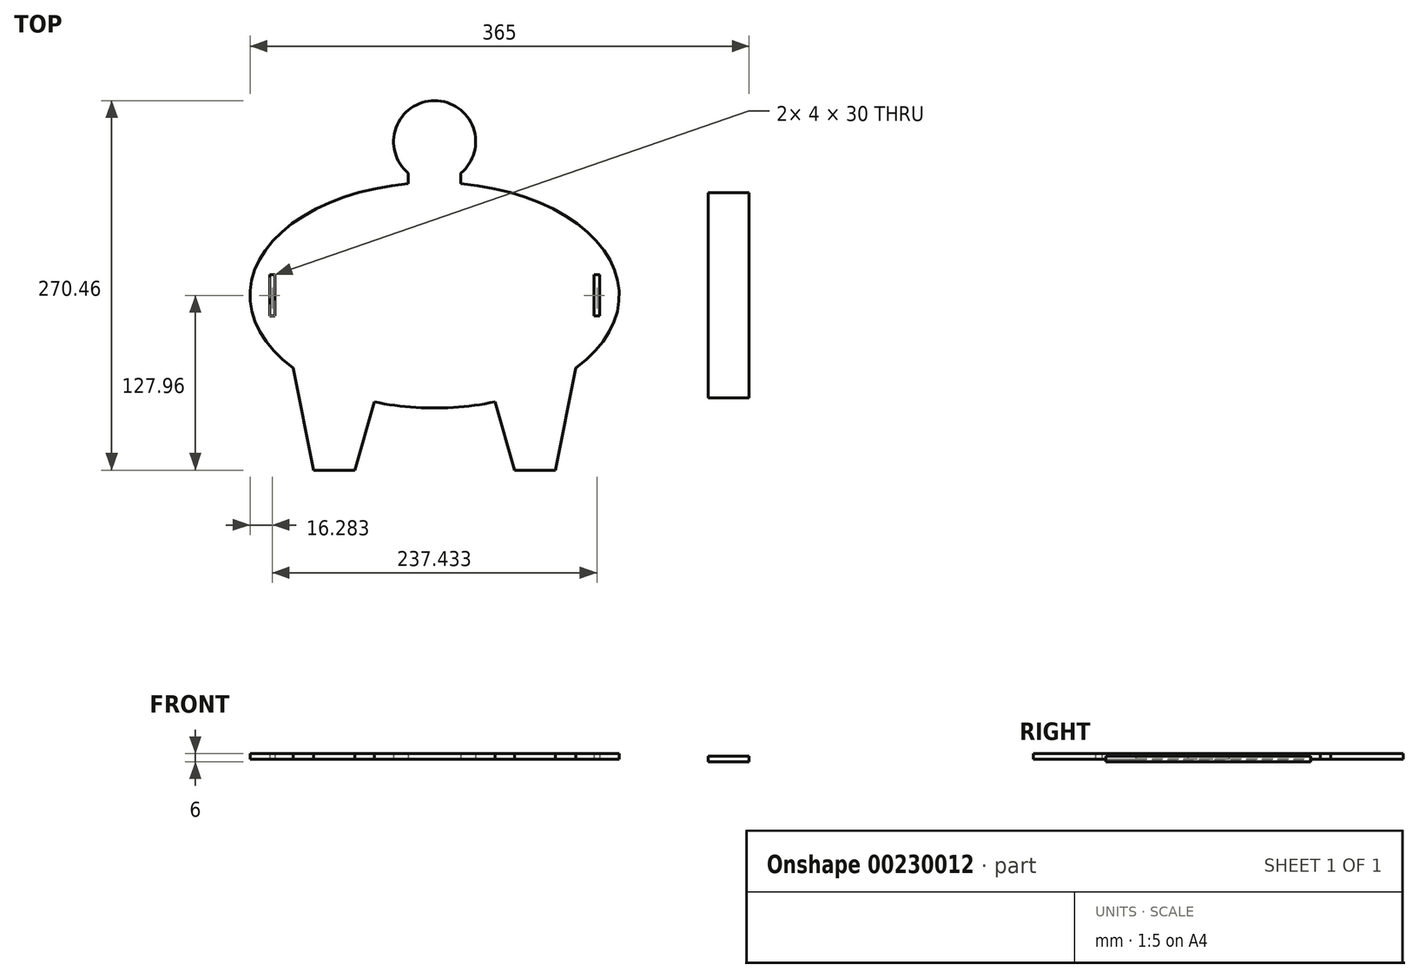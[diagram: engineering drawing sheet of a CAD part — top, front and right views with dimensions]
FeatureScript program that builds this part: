
annotation { "Feature Type Name" : "Feature", "Feature Type Description" : "" }
export const myFeature = defineFeature(function(context is Context, id is Id, definition is map)
    precondition{}
    {
        {
            var Q0;
            Q0=qCreatedBy(makeId("Top.planeOp"),FACE);
            var sketch = newSketch(context, id + "F0", { "sketchPlane" : qUnion([Q0])});
            skEllipse(sketch, "E0", {"center": v(0, 0) * mm, "majorRadius": 135 * mm, "minorRadius": 82.5 * mm, "majorAxis": v(1, 0)});
            skFitSpline(sketch, "E1.0", {"points": [v(104.96, -1.66) * mm, v(105.02, 0) * mm, v(104.96, 1.66) * mm, v(104.68, 3.9) * mm, v(103.99, 6.8) * mm, v(102.45, 10.58) * mm, v(100.05, 14.7) * mm, v(96.68, 19.09) * mm, v(92.97, 22.89) * mm, v(89.46, 25.95) * mm, v(86.54, 28.24) * mm, v(83.87, 30.13) * mm, v(81.6, 31.63) * mm, v(79.83, 32.74) * mm, v(77.99, 33.84) * mm, v(75.46, 35.27) * mm, v(72.16, 37) * mm, v(67.99, 39) * mm, v(62.15, 41.5) * mm, v(54.38, 44.35) * mm, v(44.4, 47.23) * mm, v(33.86, 49.54) * mm, v(24.7, 50.95) * mm, v(17.22, 51.75) * mm, v(11.54, 52.18) * mm, v(6.75, 52.4) * mm, v(2.9, 52.49) * mm, v(0, 52.5) * mm, v(-2.9, 52.49) * mm, v(-6.75, 52.4) * mm, v(-11.54, 52.18) * mm, v(-17.22, 51.75) * mm, v(-24.7, 50.95) * mm, v(-33.86, 49.54) * mm, v(-44.4, 47.23) * mm, v(-54.38, 44.35) * mm, v(-62.15, 41.5) * mm, v(-67.99, 39) * mm, v(-72.16, 37) * mm, v(-75.46, 35.27) * mm, v(-77.99, 33.84) * mm, v(-79.83, 32.74) * mm, v(-81.6, 31.63) * mm, v(-83.87, 30.13) * mm, v(-86.54, 28.24) * mm, v(-89.46, 25.95) * mm, v(-92.97, 22.89) * mm, v(-96.68, 19.09) * mm, v(-100.05, 14.7) * mm, v(-102.45, 10.58) * mm, v(-103.99, 6.8) * mm, v(-104.68, 3.9) * mm, v(-104.96, 1.66) * mm, v(-105.02, 0) * mm, v(-104.96, -1.66) * mm, v(-104.68, -3.9) * mm, v(-103.99, -6.8) * mm, v(-102.45, -10.58) * mm, v(-100.05, -14.7) * mm, v(-96.68, -19.09) * mm, v(-92.97, -22.89) * mm, v(-89.46, -25.95) * mm, v(-86.54, -28.24) * mm, v(-83.87, -30.13) * mm, v(-81.6, -31.63) * mm, v(-79.83, -32.74) * mm, v(-77.99, -33.84) * mm, v(-75.46, -35.27) * mm, v(-72.16, -37) * mm, v(-67.99, -39) * mm, v(-62.15, -41.5) * mm, v(-54.38, -44.35) * mm, v(-44.4, -47.23) * mm, v(-33.86, -49.54) * mm, v(-24.7, -50.95) * mm, v(-17.22, -51.75) * mm, v(-11.54, -52.18) * mm, v(-6.75, -52.4) * mm, v(-2.9, -52.49) * mm, v(0, -52.5) * mm, v(2.9, -52.49) * mm, v(6.75, -52.4) * mm, v(11.54, -52.18) * mm, v(17.22, -51.75) * mm, v(24.7, -50.95) * mm, v(33.86, -49.54) * mm, v(44.4, -47.23) * mm, v(54.38, -44.35) * mm, v(62.15, -41.5) * mm, v(67.99, -39) * mm, v(72.16, -37) * mm, v(75.46, -35.27) * mm, v(77.99, -33.84) * mm, v(79.83, -32.74) * mm, v(81.6, -31.63) * mm, v(83.87, -30.13) * mm, v(86.54, -28.24) * mm, v(89.46, -25.95) * mm, v(92.97, -22.89) * mm, v(96.68, -19.09) * mm, v(100.05, -14.7) * mm, v(102.45, -10.58) * mm, v(103.99, -6.8) * mm, v(104.68, -3.9) * mm, v(104.96, -1.66) * mm, v(105.02, 0) * mm, v(104.96, 1.66) * mm, v(104.96, -1.66) * mm]});
            skLineSegment(sketch, "E2.bottom", {"start": v(150, 150) * mm, "end": v(-150, 150) * mm});
            skLineSegment(sketch, "E2.top", {"start": v(150, -150) * mm, "end": v(-150, -150) * mm});
            skLineSegment(sketch, "E2.left", {"start": v(150, 150) * mm, "end": v(150, -150) * mm});
            skLineSegment(sketch, "E2.right", {"start": v(-150, 150) * mm, "end": v(-150, -150) * mm});
            skLineSegment(sketch, "E3", {"start": v(0, 0) * mm, "end": v(0, 150) * mm, "construction": true});
            skLineSegment(sketch, "E4.1.0", {"start": v(0, 0) * mm, "end": v(-129.9, -75) * mm, "construction": true});
            skLineSegment(sketch, "E4.2.0", {"start": v(0, 0) * mm, "end": v(129.9, -75) * mm, "construction": true});
            skCircle(sketch, "E5", {"center": v(0, 112.5) * mm, "radius": 30 * mm});
            skCircle(sketch, "E6", {"center": v(70.15, -40.5) * mm, "radius": 30 * mm});
            skLineSegment(sketch, "E7", {"start": v(0, 150) * mm, "end": v(0, -150) * mm, "construction": true});
            skCircle(sketch, "E8.MirrorC", {"center": v(-70.15, -40.5) * mm, "radius": 30 * mm});
            skLineSegment(sketch, "E9.bottom", {"start": v(-30, 50.1) * mm, "end": v(30, 50.1) * mm});
            skLineSegment(sketch, "E9.top", {"start": v(-30, -24.9) * mm, "end": v(30, -24.9) * mm});
            skLineSegment(sketch, "E9.left", {"start": v(-30, 50.1) * mm, "end": v(-30, -24.9) * mm});
            skLineSegment(sketch, "E9.right", {"start": v(30, 50.1) * mm, "end": v(30, -24.9) * mm});
            skLineSegment(sketch, "E10.top", {"start": v(103.41, -127.96) * mm, "end": v(43.41, -127.96) * mm, "construction": true});
            skLineSegment(sketch, "E10.left", {"start": v(103.41, -53.03) * mm, "end": v(103.41, -127.96) * mm, "construction": true});
            skLineSegment(sketch, "E11.trimOffspring", {"start": v(44.17, -77.96) * mm, "end": v(43.41, -127.96) * mm, "construction": true});
            skLineSegment(sketch, "E12", {"start": v(73.41, -127.96) * mm, "end": v(73.41, -69.24) * mm, "construction": true});
            skPoint(sketch, "E13", {"position": v(58.41, -127.96) * mm});
            skPoint(sketch, "E14", {"position": v(88.41, -127.96) * mm});
            skLineSegment(sketch, "E15", {"start": v(44.17, -77.96) * mm, "end": v(58.41, -127.96) * mm});
            skLineSegment(sketch, "E16", {"start": v(88.41, -127.96) * mm, "end": v(103.41, -53.03) * mm});
            skLineSegment(sketch, "E17", {"start": v(58.41, -127.96) * mm, "end": v(88.41, -127.96) * mm});
            skLineSegment(sketch, "E18.MirrorCS", {"start": v(-58.41, -127.96) * mm, "end": v(-88.41, -127.96) * mm});
            skLineSegment(sketch, "E19.MirrorCS", {"start": v(-103.41, -127.96) * mm, "end": v(-43.41, -127.96) * mm, "construction": true});
            skLineSegment(sketch, "E20.MirrorCS", {"start": v(-73.41, -127.96) * mm, "end": v(-73.41, -69.24) * mm, "construction": true});
            skLineSegment(sketch, "E21.MirrorCS", {"start": v(-44.17, -77.96) * mm, "end": v(-58.41, -127.96) * mm});
            skPoint(sketch, "E22.MirrorP", {"position": v(-58.41, -127.96) * mm});
            skLineSegment(sketch, "E23.MirrorCS", {"start": v(-44.17, -77.96) * mm, "end": v(-43.41, -127.96) * mm, "construction": true});
            skPoint(sketch, "E24.MirrorP", {"position": v(-88.41, -127.96) * mm});
            skLineSegment(sketch, "E25.MirrorCS", {"start": v(-88.41, -127.96) * mm, "end": v(-103.41, -53.03) * mm});
            skLineSegment(sketch, "E26.MirrorCS", {"start": v(-103.41, -53.03) * mm, "end": v(-103.41, -127.96) * mm, "construction": true});
            skLineSegment(sketch, "E27.bottom", {"start": v(-150, 150) * mm, "end": v(150, 150) * mm});
            skLineSegment(sketch, "E27.top", {"start": v(-150, -150) * mm, "end": v(150, -150) * mm});
            skLineSegment(sketch, "E28", {"start": v(-19.17, 89.43) * mm, "end": v(-19.17, 81.66) * mm});
            skLineSegment(sketch, "E29.MirrorCS", {"start": v(19.17, 89.43) * mm, "end": v(19.17, 81.66) * mm});
            skLineSegment(sketch, "E30.bottom", {"start": v(-116.72, 15) * mm, "end": v(-120.72, 15) * mm});
            skLineSegment(sketch, "E30.top", {"start": v(-116.72, -15) * mm, "end": v(-120.72, -15) * mm});
            skLineSegment(sketch, "E30.left", {"start": v(-116.72, 15) * mm, "end": v(-116.72, -15) * mm});
            skLineSegment(sketch, "E30.right", {"start": v(-120.72, 15) * mm, "end": v(-120.72, -15) * mm});
            skPoint(sketch, "E30.middle", {"position": v(-118.72, 0) * mm});
            skLineSegment(sketch, "E31.MirrorCS", {"start": v(116.72, -15) * mm, "end": v(120.72, -15) * mm});
            skLineSegment(sketch, "E32.MirrorCS", {"start": v(116.72, 15) * mm, "end": v(120.72, 15) * mm});
            skPoint(sketch, "E33.MirrorP", {"position": v(118.72, 0) * mm});
            skLineSegment(sketch, "E34.MirrorCS", {"start": v(120.72, 15) * mm, "end": v(120.72, -15) * mm});
            skLineSegment(sketch, "E35.MirrorCS", {"start": v(116.72, 15) * mm, "end": v(116.72, -15) * mm});
            skSolve(sketch);
        }
        {
            var Q0;
            Q0=makeQuery(id+"F0.imprint","IMPRINT",FACE,{"disambiguationData":[TD([[makeQuery(id+"F0.imprint","IMPRINT",EDGE,{"derivedFrom":sQuery(id+"F0.wireOp",EDGE,"E5")}),1.0]])]});
            var Q1;
            {var subQ0=sQuery(id+"F0.wireOp",EDGE,"E0");var subQ5=makeQuery(id+"F0.imprint","INTERSECT",VERTEX,{"derivedFrom":[subQ0,sQuery(id+"F0.wireOp",EDGE,"E25.MirrorCS")]});Q1=makeQuery(id+"F0.imprint","IMPRINT",FACE,{"disambiguationData":[TD([[makeQuery(id+"F0.imprint","IMPRINT",EDGE,{"disambiguationData":[TD([[subQ5,1.0]])],"derivedFrom":subQ0}),1.0]])]});}
            var Q2;
            {var subQ0=sQuery(id+"F0.wireOp",EDGE,"E8.MirrorC");var subQ1=sQuery(id+"F0.wireOp",EDGE,"E0");var subQ2=makeQuery(id+"F0.imprint","INTERSECT",VERTEX,{"disambiguationData":[OD(0.0)],"derivedFrom":[subQ1,subQ0]});Q2=makeQuery(id+"F0.imprint","IMPRINT",FACE,{"disambiguationData":[TD([[makeQuery(id+"F0.imprint","IMPRINT",EDGE,{"disambiguationData":[TD([[subQ2,-1.0]])],"derivedFrom":subQ1}),1.0]])]});}
            var Q3;
            {var subQ0=sQuery(id+"F0.wireOp",EDGE,"E8.MirrorC");var subQ1=sQuery(id+"F0.wireOp",EDGE,"E1.0");var subQ2=makeQuery(id+"F0.imprint","INTERSECT",VERTEX,{"disambiguationData":[OD(0.0)],"derivedFrom":[subQ1,subQ0]});Q3=makeQuery(id+"F0.imprint","IMPRINT",FACE,{"disambiguationData":[TD([[makeQuery(id+"F0.imprint","IMPRINT",EDGE,{"disambiguationData":[TD([[subQ2,-1.0]])],"derivedFrom":subQ1}),1.0]])]});}
            var Q4;
            {var subQ0=sQuery(id+"F0.wireOp",EDGE,"E9.bottom");Q4=makeQuery(id+"F0.imprint","IMPRINT",FACE,{"disambiguationData":[TD([[makeQuery(id+"F0.imprint","IMPRINT",EDGE,{"derivedFrom":subQ0}),1.0]])]});}
            var Q5;
            Q5=makeQuery(id+"F0.imprint","IMPRINT",FACE,{"disambiguationData":[TD([[makeQuery(id+"F0.imprint","IMPRINT",EDGE,{"derivedFrom":sQuery(id+"F0.wireOp",EDGE,"E9.bottom")}),-1.0]])]});
            var Q6;
            {var subQ0=sQuery(id+"F0.wireOp",EDGE,"E6");var subQ1=sQuery(id+"F0.wireOp",EDGE,"E1.0");var subQ2=makeQuery(id+"F0.imprint","INTERSECT",VERTEX,{"disambiguationData":[OD(0.0)],"derivedFrom":[subQ1,subQ0]});Q6=makeQuery(id+"F0.imprint","IMPRINT",FACE,{"disambiguationData":[TD([[makeQuery(id+"F0.imprint","IMPRINT",EDGE,{"disambiguationData":[TD([[subQ2,-1.0]])],"derivedFrom":subQ1}),1.0]])]});}
            var Q7;
            {var subQ0=sQuery(id+"F0.wireOp",EDGE,"E6");var subQ1=sQuery(id+"F0.wireOp",EDGE,"E0");var subQ2=makeQuery(id+"F0.imprint","INTERSECT",VERTEX,{"disambiguationData":[OD(0.0)],"derivedFrom":[subQ1,subQ0]});Q7=makeQuery(id+"F0.imprint","IMPRINT",FACE,{"disambiguationData":[TD([[makeQuery(id+"F0.imprint","IMPRINT",EDGE,{"disambiguationData":[TD([[subQ2,-1.0]])],"derivedFrom":subQ1}),1.0]])]});}
            var Q8;
            {var subQ0=sQuery(id+"F0.wireOp",EDGE,"E6");var subQ1=sQuery(id+"F0.wireOp",EDGE,"E0");var subQ2=makeQuery(id+"F0.imprint","INTERSECT",VERTEX,{"disambiguationData":[OD(0.0)],"derivedFrom":[subQ1,subQ0]});Q8=makeQuery(id+"F0.imprint","IMPRINT",FACE,{"disambiguationData":[TD([[makeQuery(id+"F0.imprint","IMPRINT",EDGE,{"disambiguationData":[TD([[subQ2,-1.0]])],"derivedFrom":subQ1}),-1.0]])]});}
            var Q9;
            {var subQ0=sQuery(id+"F0.wireOp",EDGE,"E8.MirrorC");var subQ1=sQuery(id+"F0.wireOp",EDGE,"E0");var subQ2=makeQuery(id+"F0.imprint","INTERSECT",VERTEX,{"disambiguationData":[OD(0.0)],"derivedFrom":[subQ1,subQ0]});Q9=makeQuery(id+"F0.imprint","IMPRINT",FACE,{"disambiguationData":[TD([[makeQuery(id+"F0.imprint","IMPRINT",EDGE,{"disambiguationData":[TD([[subQ2,-1.0]])],"derivedFrom":subQ1}),-1.0]])]});}
            var Q10;
            Q10=makeQuery(id+"F0.imprint","IMPRINT",FACE,{"disambiguationData":[TD([[makeQuery(id+"F0.imprint","IMPRINT",EDGE,{"derivedFrom":sQuery(id+"F0.wireOp",EDGE,"E18.MirrorCS")}),-1.0]])]});
            var Q11;
            {var subQ0=sQuery(id+"F0.wireOp",EDGE,"E15");Q11=makeQuery(id+"F0.imprint","IMPRINT",FACE,{"disambiguationData":[TD([[makeQuery(id+"F0.imprint","IMPRINT",EDGE,{"derivedFrom":subQ0}),1.0]])]});}
            var Q12;
            {var subQ5=sQuery(id+"F0.wireOp",EDGE,"E0");var subQ8=makeQuery(id+"F0.imprint","INTERSECT",VERTEX,{"derivedFrom":[subQ5,sQuery(id+"F0.wireOp",EDGE,"E21.MirrorCS")]});Q12=makeQuery(id+"F0.imprint","IMPRINT",FACE,{"disambiguationData":[TD([[makeQuery(id+"F0.imprint","IMPRINT",EDGE,{"disambiguationData":[TD([[subQ8,1.0]])],"derivedFrom":subQ5}),1.0]])]});}
            var Q13;
            {var subQ0=sQuery(id+"F0.wireOp",EDGE,"E28");Q13=makeQuery(id+"F0.imprint","IMPRINT",FACE,{"disambiguationData":[TD([[makeQuery(id+"F0.imprint","IMPRINT",EDGE,{"derivedFrom":subQ0}),1.0]])]});}
            var Q14;
            {var subQ0=sQuery(id+"F0.wireOp",EDGE,"E29.MirrorCS");Q14=makeQuery(id+"F0.imprint","IMPRINT",FACE,{"disambiguationData":[TD([[makeQuery(id+"F0.imprint","IMPRINT",EDGE,{"derivedFrom":subQ0}),-1.0]])]});}
            extrude(context, id + "F1", {"entities" : qUnion([Q0, Q1, Q2, Q3, Q4, Q5, Q6, Q7, Q8, Q9, Q10, Q11, Q12, Q13, Q14]), "depth" : 4 * mm, "offsetDistance" : 25 * mm});
        }
        {
            var Q0;
            Q0=qCreatedBy(makeId("Right.planeOp"),FACE);
            cPlane(context, id + "F2", {"entities" : qUnion([Q0]), "cplaneType" : CPlaneType.OFFSET, "offset" : 200 * mm, "width" : 150 * mm, "height" : 150 * mm});
        }
        {
            var Q0;
            Q0=qCreatedBy(id+"F2.planeOp",FACE);
            var sketch = newSketch(context, id + "F3", { "sketchPlane" : qUnion([Q0])});
            skLineSegment(sketch, "E36.bottom", {"start": v(75, -2) * mm, "end": v(-75, -2) * mm});
            skLineSegment(sketch, "E36.top", {"start": v(75, 2) * mm, "end": v(-75, 2) * mm});
            skLineSegment(sketch, "E36.left", {"start": v(75, -2) * mm, "end": v(75, 2) * mm});
            skLineSegment(sketch, "E36.right", {"start": v(-75, -2) * mm, "end": v(-75, 2) * mm});
            skPoint(sketch, "E36.middle", {"position": v(0, 0) * mm});
            skSolve(sketch);
        }
        {
            var Q0;
            Q0=makeQuery(id+"F3.imprint","IMPRINT",FACE,{"disambiguationData":[TD([[makeQuery(id+"F3.imprint","IMPRINT",EDGE,{"derivedFrom":sQuery(id+"F3.wireOp",EDGE,"E36.bottom")}),-1.0]])]});
            extrude(context, id + "F4", {"entities" : qUnion([Q0]), "depth" : 30 * mm, "offsetDistance" : 25 * mm});
        }
    });
